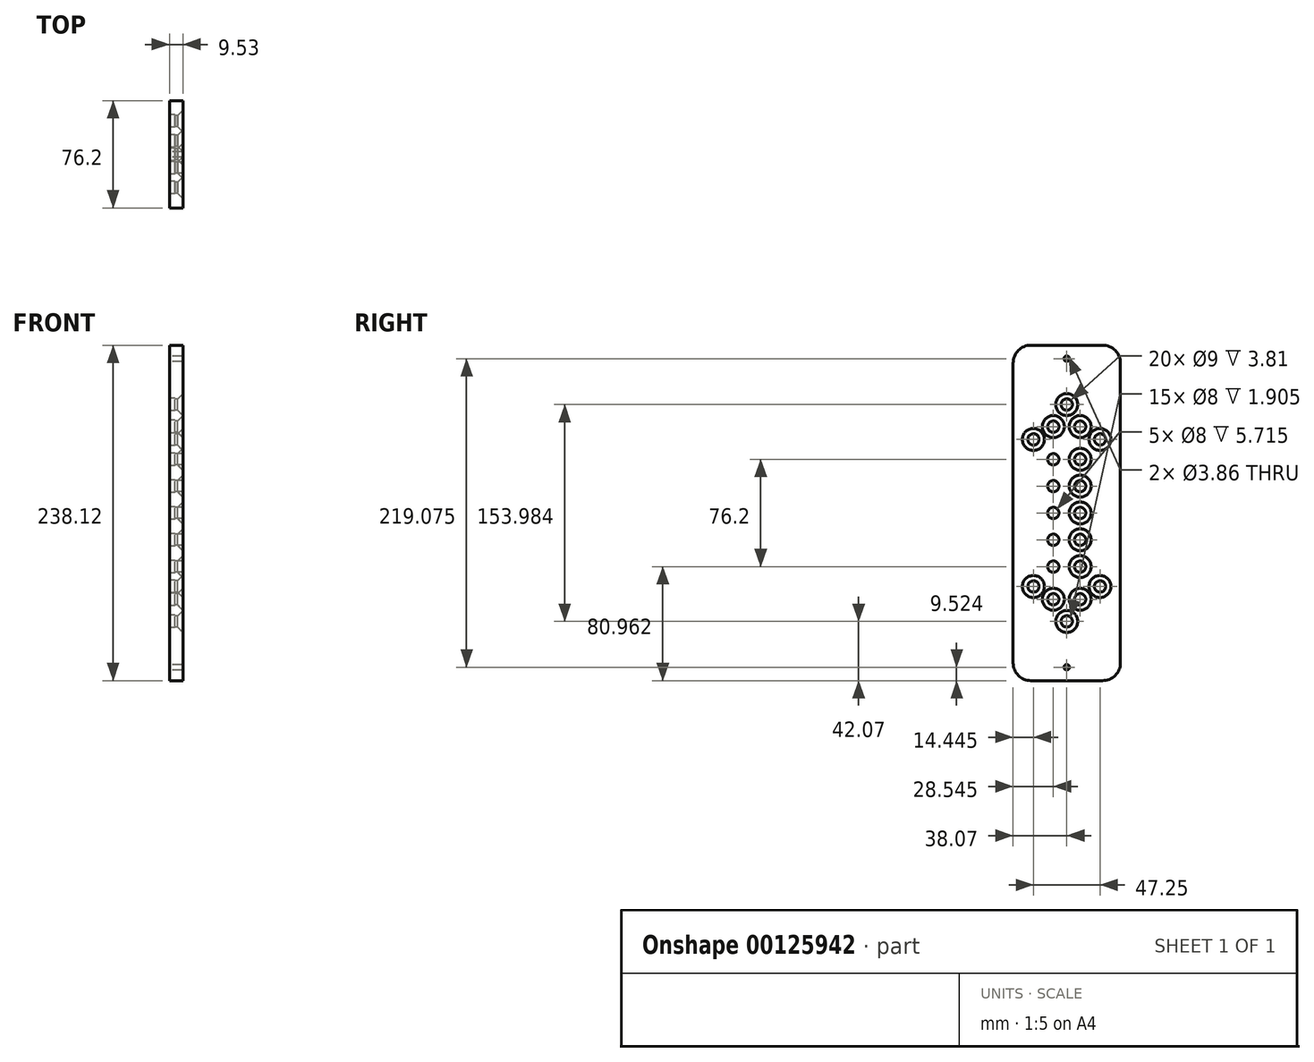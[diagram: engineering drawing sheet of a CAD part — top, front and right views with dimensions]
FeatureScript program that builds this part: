
annotation { "Feature Type Name" : "Feature", "Feature Type Description" : "" }
export const myFeature = defineFeature(function(context is Context, id is Id, definition is map)
    precondition{}
    {
        {
            var Q0;
            Q0=qCreatedBy(makeId("Right.planeOp"),FACE);
            var sketch = newSketch(context, id + "F0", { "sketchPlane" : qUnion([Q0])});
            skLineSegment(sketch, "E0", {"start": v(-38.07, 112.92) * mm, "end": v(-38.07, -99.8) * mm});
            skArc(sketch, "E1", {"start": v(-38.07, 112.92) * mm, "mid": v(-34.35, 121.9) * mm, "end": v(-25.37, 125.62) * mm});
            skLineSegment(sketch, "E2", {"start": v(-25.37, 125.62) * mm, "end": v(0.03, 125.62) * mm});
            skArc(sketch, "E3", {"start": v(-38.07, -99.8) * mm, "mid": v(-34.35, -108.78) * mm, "end": v(-25.37, -112.5) * mm});
            skLineSegment(sketch, "E4", {"start": v(-25.37, -112.5) * mm, "end": v(0.03, -112.5) * mm});
            skLineSegment(sketch, "E5.MirrorCS", {"start": v(25.43, -112.5) * mm, "end": v(0.03, -112.5) * mm});
            skArc(sketch, "E6.MirrorCS", {"start": v(38.13, -99.8) * mm, "mid": v(34.4, -108.78) * mm, "end": v(25.43, -112.5) * mm});
            skLineSegment(sketch, "E7.MirrorCS", {"start": v(25.43, 125.62) * mm, "end": v(0.03, 125.62) * mm});
            skLineSegment(sketch, "E8.MirrorCS", {"start": v(38.13, 112.92) * mm, "end": v(38.13, -99.8) * mm});
            skArc(sketch, "E9.MirrorCS", {"start": v(38.13, 112.92) * mm, "mid": v(34.4, 121.9) * mm, "end": v(25.43, 125.62) * mm});
            skCircle(sketch, "E10", {"center": v(0, 116.1) * mm, "radius": 1.93 * mm});
            skCircle(sketch, "E11", {"center": v(0, -102.98) * mm, "radius": 1.93 * mm});
            skLineSegment(sketch, "E12", {"start": v(-26.65, 6.56) * mm, "end": v(25.9, 6.56) * mm, "construction": true});
            skCircle(sketch, "E13", {"center": v(-9.53, 6.56) * mm, "radius": 4 * mm});
            skLineSegment(sketch, "E14.direction1", {"start": v(-9.53, 6.56) * mm, "end": v(11.24, 6.56) * mm, "construction": true});
            skLineSegment(sketch, "E15", {"start": v(-9.53, -102.98) * mm, "end": v(-9.53, 116.1) * mm, "construction": true});
            skCircle(sketch, "E16", {"center": v(-9.52, 25.61) * mm, "radius": 4 * mm});
            skCircle(sketch, "E17", {"center": v(-9.52, 44.66) * mm, "radius": 4 * mm});
            skCircle(sketch, "E18", {"center": v(-9.52, -12.49) * mm, "radius": 4 * mm});
            skCircle(sketch, "E19", {"center": v(-9.52, -31.54) * mm, "radius": 4 * mm});
            skLineSegment(sketch, "E20", {"start": v(0, 83.55) * mm, "end": v(0, -96.2) * mm, "construction": true});
            skLineSegment(sketch, "E21.MirrorCS", {"start": v(9.53, -102.98) * mm, "end": v(9.52, 116.1) * mm, "construction": true});
            skCircle(sketch, "E22.MirrorC", {"center": v(9.52, 44.66) * mm, "radius": 4 * mm});
            skCircle(sketch, "E23.MirrorC", {"center": v(9.52, 25.61) * mm, "radius": 4 * mm});
            skCircle(sketch, "E24.MirrorC", {"center": v(9.53, 6.56) * mm, "radius": 4 * mm});
            skCircle(sketch, "E25.MirrorC", {"center": v(9.53, -12.49) * mm, "radius": 4 * mm});
            skCircle(sketch, "E26.MirrorC", {"center": v(9.53, -31.54) * mm, "radius": 4 * mm});
            skLineSegment(sketch, "E27", {"start": v(9.52, 25.61) * mm, "end": v(-29.96, 65.1) * mm, "construction": true});
            skCircle(sketch, "E28", {"center": v(-23.62, 58.76) * mm, "radius": 4 * mm});
            skCircle(sketch, "E29", {"center": v(0, 83.55) * mm, "radius": 4 * mm});
            skCircle(sketch, "E30", {"center": v(-9.52, 67.86) * mm, "radius": 4 * mm});
            skCircle(sketch, "E31.MirrorC", {"center": v(23.62, 58.76) * mm, "radius": 4 * mm});
            skCircle(sketch, "E32.MirrorC", {"center": v(9.52, 67.86) * mm, "radius": 4 * mm});
            skCircle(sketch, "E33.MirrorC", {"center": v(23.62, -45.64) * mm, "radius": 4 * mm});
            skCircle(sketch, "E34.MirrorC", {"center": v(9.53, -54.73) * mm, "radius": 4 * mm});
            skCircle(sketch, "E35.MirrorC", {"center": v(0, -70.43) * mm, "radius": 4 * mm});
            skCircle(sketch, "E36.MirrorC", {"center": v(-9.53, -54.73) * mm, "radius": 4 * mm});
            skCircle(sketch, "E37.MirrorC", {"center": v(-23.62, -45.64) * mm, "radius": 4 * mm});
            skSolve(sketch);
        }
        {
            var Q0;
            Q0 = qSketchRegion(id + "F0", true);
            extrude(context, id + "F1", {"entities" : qUnion([Q0]), "depth" : 9.52 * mm});
        }
        {
            var Q0;
            Q0=makeQuery(id+"F1.opExtrude","CAP_EDGE",EDGE,{"disambiguationData":[OSD([sQuery(id+"F0.wireOp",EDGE,"E29")])],"isStart":false});
            var Q1;
            Q1=makeQuery(id+"F1.opExtrude","CAP_EDGE",EDGE,{"disambiguationData":[OSD([sQuery(id+"F0.wireOp",EDGE,"E32.MirrorC")])],"isStart":false});
            var Q2;
            Q2=makeQuery(id+"F1.opExtrude","CAP_EDGE",EDGE,{"disambiguationData":[OSD([sQuery(id+"F0.wireOp",EDGE,"E31.MirrorC")])],"isStart":false});
            var Q3;
            Q3=makeQuery(id+"F1.opExtrude","CAP_EDGE",EDGE,{"disambiguationData":[OSD([sQuery(id+"F0.wireOp",EDGE,"E30")])],"isStart":false});
            var Q4;
            Q4=makeQuery(id+"F1.opExtrude","CAP_EDGE",EDGE,{"disambiguationData":[OSD([sQuery(id+"F0.wireOp",EDGE,"E28")])],"isStart":false});
            var Q5;
            Q5=makeQuery(id+"F1.opExtrude","CAP_EDGE",EDGE,{"disambiguationData":[OSD([sQuery(id+"F0.wireOp",EDGE,"E17")])],"isStart":false});
            var Q6;
            Q6=makeQuery(id+"F1.opExtrude","CAP_EDGE",EDGE,{"disambiguationData":[OSD([sQuery(id+"F0.wireOp",EDGE,"E22.MirrorC")])],"isStart":false});
            var Q7;
            Q7=makeQuery(id+"F1.opExtrude","CAP_EDGE",EDGE,{"disambiguationData":[OSD([sQuery(id+"F0.wireOp",EDGE,"E16")])],"isStart":false});
            var Q8;
            Q8=makeQuery(id+"F1.opExtrude","CAP_EDGE",EDGE,{"disambiguationData":[OSD([sQuery(id+"F0.wireOp",EDGE,"E13")])],"isStart":false});
            var Q9;
            Q9=makeQuery(id+"F1.opExtrude","CAP_EDGE",EDGE,{"disambiguationData":[OSD([sQuery(id+"F0.wireOp",EDGE,"E18")])],"isStart":false});
            var Q10;
            Q10=makeQuery(id+"F1.opExtrude","CAP_EDGE",EDGE,{"disambiguationData":[OSD([sQuery(id+"F0.wireOp",EDGE,"E19")])],"isStart":false});
            var Q11;
            Q11=makeQuery(id+"F1.opExtrude","CAP_EDGE",EDGE,{"disambiguationData":[OSD([sQuery(id+"F0.wireOp",EDGE,"E26.MirrorC")])],"isStart":false});
            var Q12;
            Q12=makeQuery(id+"F1.opExtrude","CAP_EDGE",EDGE,{"disambiguationData":[OSD([sQuery(id+"F0.wireOp",EDGE,"E25.MirrorC")])],"isStart":false});
            var Q13;
            Q13=makeQuery(id+"F1.opExtrude","CAP_EDGE",EDGE,{"disambiguationData":[OSD([sQuery(id+"F0.wireOp",EDGE,"E24.MirrorC")])],"isStart":false});
            var Q14;
            Q14=makeQuery(id+"F1.opExtrude","CAP_EDGE",EDGE,{"disambiguationData":[OSD([sQuery(id+"F0.wireOp",EDGE,"E23.MirrorC")])],"isStart":false});
            var Q15;
            Q15=makeQuery(id+"F1.opExtrude","CAP_EDGE",EDGE,{"disambiguationData":[OSD([sQuery(id+"F0.wireOp",EDGE,"E33.MirrorC")])],"isStart":false});
            var Q16;
            Q16=makeQuery(id+"F1.opExtrude","CAP_EDGE",EDGE,{"disambiguationData":[OSD([sQuery(id+"F0.wireOp",EDGE,"E34.MirrorC")])],"isStart":false});
            var Q17;
            Q17=makeQuery(id+"F1.opExtrude","CAP_EDGE",EDGE,{"disambiguationData":[OSD([sQuery(id+"F0.wireOp",EDGE,"E36.MirrorC")])],"isStart":false});
            var Q18;
            Q18=makeQuery(id+"F1.opExtrude","CAP_EDGE",EDGE,{"disambiguationData":[OSD([sQuery(id+"F0.wireOp",EDGE,"E37.MirrorC")])],"isStart":false});
            var Q19;
            Q19=makeQuery(id+"F1.opExtrude","CAP_EDGE",EDGE,{"disambiguationData":[OSD([sQuery(id+"F0.wireOp",EDGE,"E35.MirrorC")])],"isStart":false});
            chamfer(context, id + "F2", {"entities" : qUnion([Q0, Q1, Q2, Q3, Q4, Q5, Q6, Q7, Q8, Q9, Q10, Q11, Q12, Q13, Q14, Q15, Q16, Q17, Q18, Q19]), "width" : 3.8 * mm, "tangentPropagation" : true});
        }
        {
            var Q0;
            Q0=qCreatedBy(makeId("Right.planeOp"),FACE);
            var sketch = newSketch(context, id + "F3", { "sketchPlane" : qUnion([Q0])});
            skCircle(sketch, "E38", {"center": v(0, -70.43) * mm, "radius": 4.5 * mm});
            skCircle(sketch, "E39", {"center": v(0, 83.55) * mm, "radius": 4.5 * mm});
            skCircle(sketch, "E40", {"center": v(9.53, -31.54) * mm, "radius": 4.5 * mm});
            skCircle(sketch, "E41.0.1.0", {"center": v(9.53, -12.49) * mm, "radius": 4.5 * mm});
            skCircle(sketch, "E41.0.2.0", {"center": v(9.53, 6.56) * mm, "radius": 4.5 * mm});
            skCircle(sketch, "E41.0.3.0", {"center": v(9.53, 25.61) * mm, "radius": 4.5 * mm});
            skCircle(sketch, "E41.0.4.0", {"center": v(9.53, 44.66) * mm, "radius": 4.5 * mm});
            skCircle(sketch, "E41.1.0.0", {"center": v(-9.52, -31.54) * mm, "radius": 4.5 * mm});
            skCircle(sketch, "E41.1.1.0", {"center": v(-9.52, -12.49) * mm, "radius": 4.5 * mm});
            skCircle(sketch, "E41.1.2.0", {"center": v(-9.52, 6.56) * mm, "radius": 4.5 * mm});
            skCircle(sketch, "E41.1.3.0", {"center": v(-9.52, 25.61) * mm, "radius": 4.5 * mm});
            skCircle(sketch, "E41.1.4.0", {"center": v(-9.52, 44.66) * mm, "radius": 4.5 * mm});
            skLineSegment(sketch, "E41.direction1", {"start": v(9.53, -31.54) * mm, "end": v(-9.52, -31.54) * mm, "construction": true});
            skLineSegment(sketch, "E41.direction2", {"start": v(9.53, -31.54) * mm, "end": v(9.53, -12.49) * mm, "construction": true});
            skLineSegment(sketch, "E42", {"start": v(-23.34, 6.56) * mm, "end": v(24.22, 6.56) * mm, "construction": true});
            skLineSegment(sketch, "E43", {"start": v(0, -44.93) * mm, "end": v(0, 57.47) * mm, "construction": true});
            skCircle(sketch, "E44", {"center": v(23.62, 58.76) * mm, "radius": 4.5 * mm});
            skCircle(sketch, "E45", {"center": v(9.52, 67.86) * mm, "radius": 4.5 * mm});
            skCircle(sketch, "E46.MirrorC", {"center": v(-23.62, 58.76) * mm, "radius": 4.5 * mm});
            skCircle(sketch, "E47.MirrorC", {"center": v(-9.52, 67.86) * mm, "radius": 4.5 * mm});
            skCircle(sketch, "E48.MirrorC", {"center": v(23.62, -45.64) * mm, "radius": 4.5 * mm});
            skCircle(sketch, "E49.MirrorC", {"center": v(9.52, -54.73) * mm, "radius": 4.5 * mm});
            skCircle(sketch, "E50.MirrorC", {"center": v(-9.52, -54.73) * mm, "radius": 4.5 * mm});
            skCircle(sketch, "E51.MirrorC", {"center": v(-23.62, -45.64) * mm, "radius": 4.5 * mm});
            skSolve(sketch);
        }
        {
            var Q0;
            Q0 = qSketchRegion(id + "F3", true);
            extrude(context, id + "F4", {"entities" : qUnion([Q0]), "operationType" : NewBodyOperationType.REMOVE, "depth" : 3.8 * mm});
        }
    });
